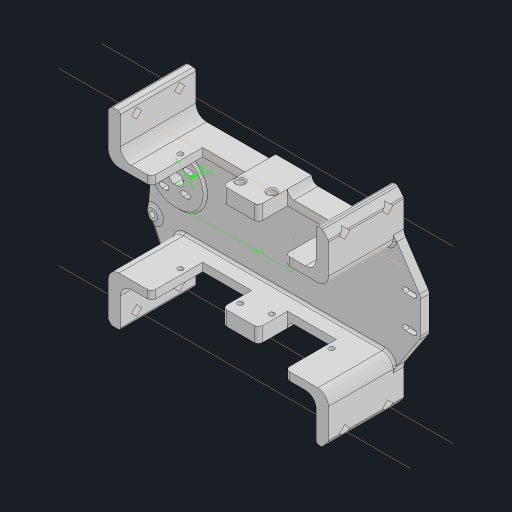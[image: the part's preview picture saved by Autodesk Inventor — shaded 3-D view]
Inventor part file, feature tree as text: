
AUTODESK INVENTOR PART (.ipt)
format: ipt  version: 2023.2 (Build 272271030, 271C)  size: 1,597,440 bytes
history: native  units: mm
features: extrude x17, sketch x17, projected_geometry x14, fillet x9, other x4, hole x1, chamfer x1, mirror x1
ambient origin geometry x8: Origin, YZ Plane, XZ Plane, XY Plane, X Axis, Y Axis, Z Axis, Center Point
bodies: Solid1 (feature_tree)
feature tree (64):
  extrude  "Extrusion1"  Depth=24.0mm
  extrude  "Extrusion2"  Depth=101.0mm
  extrude  "Extrusion3"  Depth=18.2mm
  extrude  "Extrusion4"  Depth=16.5mm
  other  "Work Axis7"
  other  "Work Axis8"
  other  "Work Axis9"
  other  "Work Axis10"
  extrude  "Extrusion7"  Depth=40.0mm
  hole  "Hole1"  [1 undecoded]
  extrude  "Extrusion8"  Depth=5.0mm
  extrude  "Extrusion9"  Depth=5.0mm
  extrude  "Extrusion10"  Depth=35.0mm
  fillet  "Fillet2"  Radius=3.6mm
  sketch  "Sketch15"  dims[d25=3.6mm d26=4.0mm d27=0.0mm]
  extrude  "Extrusion12"  Depth=4.0mm TaperAngle=0.0deg
  extrude  "Extrusion13"  Depth=1.5mm
  extrude  "Extrusion11"  Depth=21.2mm
  extrude  "Extrusion14"  Depth=11.2mm
  fillet  "Fillet4"  Radius=11.2mm
  extrude  "Extrusion15"  Depth=22.7mm
  fillet  "Fillet5"  Radius=27.8mm
  fillet  "Fillet6"  [1 undecoded]
  fillet  "Fillet7"  Radius=4.5mm
  fillet  "Fillet8"  Radius=16.0mm
  fillet  "Fillet9"  Radius=16.0mm
  fillet  "Fillet10"  Radius=12.0mm
  extrude  "Extrusion17"  Depth=3.0mm
  extrude  "Extrusion18"  Depth=35.0mm
  chamfer  "Chamfer1"  [1 undecoded]
  mirror  "Mirror1"
  fillet  "Fillet11"  Radius=0.0mm
  extrude  "Extrusion20"  Depth=3.0mm
  extrude  "Extrusion21"  Depth=3.0mm
  sketch  "Sketch4"  dims[d0=135.0mm d1=24.0mm]
  projected_geometry  "Projected Loop1"
  sketch  "Sketch5"  dims[d2=101.0mm d6=101.0mm]
  projected_geometry  "Projected Loop2"
  sketch  "Sketch6"  dims[d8=22.5mm d9=18.2mm]
  projected_geometry  "Projected Loop3"
  projected_geometry  "Projected Loop4"
  sketch  "Sketch9"  dims[d10=16.5mm d11=16.5mm]
  sketch  "Sketch10"  dims[d14=33.0mm d15=40.0mm]
  sketch  "Sketch11"  dims[d16=26.0mm d17=32.0mm]
  sketch  "Sketch12"  dims[d18=3.6mm d19=5.0mm]
  sketch  "Sketch13"  dims[d20=5.0mm d21=5.0mm]
  projected_geometry  "Projected Loop5"
  sketch  "Sketch14"  dims[d22=20.0mm d23=35.0mm d24=3.6mm]
  sketch  "Sketch16"  dims[d28=1.5mm d29=1.5mm]
  sketch  "Sketch17"  dims[d30=42.4mm d31=21.2mm]
  projected_geometry  "Projected Loop6"
  sketch  "Sketch18"  dims[d32=31.0mm d33=0.0mm d34=35.0mm d35=11.2mm]
  projected_geometry  "Projected Loop7"
  sketch  "Sketch21"  dims[d36=22.7mm d39=2.5mm d40=27.8mm d41=0.0mm d42=0.0mm d43=4.5mm d44=16.0mm d45=16.0mm d46=12.0mm]
  projected_geometry  "Projected Loop9"
  sketch  "Sketch22"  dims[d47=3.0mm d48=3.4mm]
  sketch  "Sketch25"  dims[d49=20.0mm d50=35.0mm]
  projected_geometry  "Projected Loop18"
  projected_geometry  "Projected Loop19"
  projected_geometry  "Projected Loop20"
  projected_geometry  "Projected Loop21"
  sketch  "Sketch26"  dims[d51=7.5mm d53=0.0mm d54=0.0mm d55=0.0mm d56=18.5mm d57=20.0mm d58=20.0mm d69=5.0mm d70=64.5mm d71=64.5mm d72=10.0mm d73=0.5mm d74=0.0mm d75=2.5mm d76=6.0mm d77=5.5mm d78=2.0mm d79=90.0deg d80=8.0mm d81=20.594885mm d84=6.0mm d85=6.0mm d86=133.539999mm d87=137.435415mm d88=0.104584mm d89=49.5mm d90=12.0mm d91=16.0mm d92=45.0deg d93=1.0mm d94=2.5mm d95=0.0mm d96=0.0mm d97=5.0mm d98=5.0mm d99=2.0mm d100=0.0mm d101=1.0mm d102=5.0mm d103=0.0mm d104=0.0mm d105=1.0mm d107=0.0mm d108=0.0mm d109=2.5mm d110=2.5mm d111=4.0mm d112=15.0mm d113=7.5mm d114=58.0mm d116=10.0mm d117=0.0mm d118=2.5mm d119=2.0mm d120=0.0mm d121=6.0mm d122=7.0mm d123=7.0mm d124=1.0mm d125=23.0mm d126=1.0mm d127=0.0mm d128=5.0mm d129=6.0mm d130=1.0mm d131=0.0mm d132=5.0mm d133=5.0mm d134=1.0mm d135=2.0mm d136=1.1mm d137=2.0mm d141=3.0mm d142=0.0mm d143=3.7mm d144=3.7mm d145=3.5mm d146=0.0mm d147=0.5mm d148=2.0mm d149=45.0deg d150=3.0mm d153=0.0mm d154=0.0mm d155=4.0mm d156=0.0mm]
  projected_geometry  "Projected Loop22"
  projected_geometry  "Projected Loop23"
note: 3 required parameter values undecoded (feature->parameter linkage not recoverable at this tier; creation-order binding heuristic only, values carry confidence <= 0.55)
